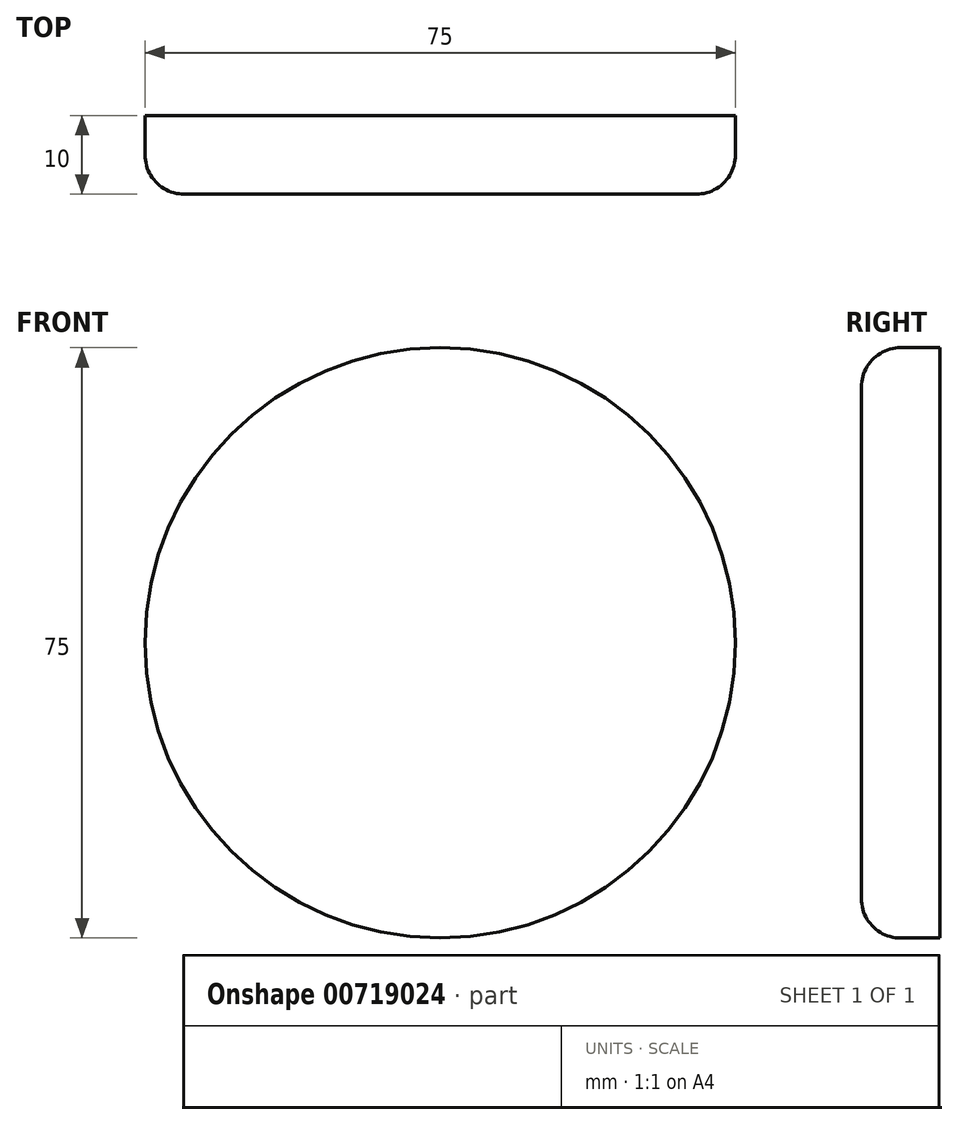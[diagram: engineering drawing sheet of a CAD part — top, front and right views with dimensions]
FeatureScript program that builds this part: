
annotation { "Feature Type Name" : "Feature", "Feature Type Description" : "" }
export const myFeature = defineFeature(function(context is Context, id is Id, definition is map)
    precondition{}
    {
        {
            var Q0;
            Q0=qCreatedBy(makeId("Front.planeOp"),FACE);
            var sketch = newSketch(context, id + "F0", { "sketchPlane" : qUnion([Q0])});
            skCircle(sketch, "E0", {"center": v(0, 0) * mm, "radius": 37.5 * mm});
            skSolve(sketch);
        }
        {
            var Q0;
            Q0=makeQuery(id+"F0.imprint","IMPRINT",FACE,{"disambiguationData":[TD([[makeQuery(id+"F0.imprint","IMPRINT",EDGE,{"derivedFrom":sQuery(id+"F0.wireOp",EDGE,"E0")}),1.0]])]});
            extrude(context, id + "F1", {"entities" : qUnion([Q0]), "depth" : 5 * mm, "offsetDistance" : 25 * mm, "hasSecondDirection" : true, "secondDirectionOppositeDirection" : true, "secondDirectionDepth" : 5 * mm});
        }
        {
            var Q0;
            Q0=makeQuery(id+"F1.opExtrude","CAP_FACE",FACE,{"disambiguationData":[OSD([sQuery(id+"F0.wireOp",EDGE,"E0")])],"isStart":false});
            fillet(context, id + "F2", {"entities" : qUnion([Q0]), "radius" : 5 * mm, "tangentPropagation" : true, "allowEdgeOverflow" : false});
        }
    });
